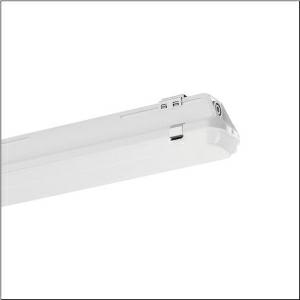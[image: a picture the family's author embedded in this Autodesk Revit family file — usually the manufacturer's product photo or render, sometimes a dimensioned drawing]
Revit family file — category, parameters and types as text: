
# Revit family: monsun_r__12_51fp10mp480h_34fc
name_source: partatom
category: Lighting Fixtures
units: mm (PartAtom-declared; Revit-internal decimal feet)

## family parameters
Cut with Voids When Loaded = No
Host = Face
Light Source = No
Part Type = Normal
Room Calculation Point = No
Round Connector Dimension = Use Diameter
Shared = No

## types (1)
- --- (1 x LED, 8070 lm, 45.4 W, 4000K)
    Apparent Load = 45 VA
    CIE Flux Codes = 47 77 93 94 100
    Color Rendering = 80
    Color Temperature = 4000K
    Default Elevation = 1800 mm
    Description = Monsun® 12, damp-proof luminaire, chain hanger, primary optical cover: enclosure, of PMMA, light emission: direct distribution, primary light characteristic: symmetric, installation type: suspended mounting, surface-mounted, horizontal mounting, vertical mounting, LED rated luminous flux: 8.070 lm, light colour: 840, colour temperature: 4000K, control gear: ECG, with terminal, 3-pole, max. 2.5mm², mains connection: 220..240V, AC, 50/60Hz, rated input power: 45W, luminaire housing, of glass-fibre reinforced polyester, uncoated, bright grey, length: 1.590 mm, width: 90 mm, height: 88mm, clip for enclosure, of stainless steel (V2A), ceiling mounting element, of stainless steel (V2A), chain hanger, of stainless steel (V2A), protection rating (complete): IP66, insulation class (complete): insulation class I (protective earthing), certification: CE, ENEC, VDE, protection symbol: D, impact resistance: IK04, permissible ambient temperature for indoor applications: -35..+40°C, standard: EN 50419, EN 60598-2-1, no direct snow, no direct sun, no direct rain, for indoor or canopied outdoor use, corresponds to IFS (International Featured Standards) requirements for safety and quality in the food industry, for animal farming (ammonia tested): for use in cowhouse, pig house, horse-stables... (not for use in poultry stables), AT max for animal farming = 40°C, packaging unit: 1 piece
    Height = 89 mm
    Lamp = 1 x LED
    Lamp Light Flux = 8070 lm
    Lamp Power = 45.4 W
    Lamp count = 1
    Length = 1590 mm
    Luminous efficacy = 178 lm/W
    Manufacturer = Siteco
    ModVariant = No
    Model = 51FP10MP480H
    Mounting Place = Ceiling
    Mounting Type = Pendant
    Number of Poles = 1
    OnlyDefault = Yes
    Power Factor = 1
    Product Name = Monsun® 12
    Product group = damp-proof luminaire | ceiling pendant
    ProductGroupID = 908
    Protection Class = Protection class I
    Protection Degree = IP 66
    RLX_Detail_Level = 1
    RlxData = <blob elided: 89633 chars, md5=14a8cddf>
    Socket = socket
    Standby Power = 0 W
    System Light Flux = 8070 lm
    System Power = 45 W
    Type Comments = factory setting: luminous flux: 100 % | (A | C | E) | 105 mA
    Type Image = l_1004748.jpg
    URL = http://relux.com
    VarID = @adj_136481
    Voltage = 0 V
    Weight = 0.00 kg
    Width = 90 mm

## geometry (parser evidence)
native form markers: Blend x4, Sweep x13
no freeform markers — native parametric forms only
